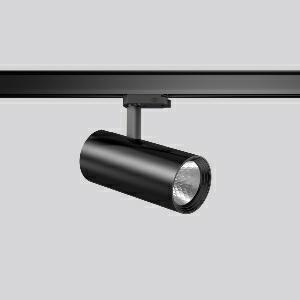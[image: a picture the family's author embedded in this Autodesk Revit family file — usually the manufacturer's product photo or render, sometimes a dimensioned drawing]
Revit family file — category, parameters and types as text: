
# Revit family: deecos_s_mini_742197_003_3_7693
name_source: partatom
category: Lighting Fixtures
units: mm (PartAtom-declared; Revit-internal decimal feet)

## family parameters
Cut with Voids When Loaded = No
Host = Face
Light Source = No
Part Type = Normal
Room Calculation Point = No
Round Connector Dimension = Use Diameter
Shared = No

## types (1)
- DEECOS S mini (1 x LED Modul 935, 2650 lm, 3500)
    Apparent Load = 20 VA
    Approval mark = CE
    CIE Flux Codes = 95 99 100 100 100
    Color Rendering = 92
    Color Temperature = 3500
    Default Elevation = 1800 mm
    Description = Series: DEECOS S mini
LED surface-mounted projector in modern design with no visible cooling ribs. Housing: die-cast aluminium, powder-coated. Rotation range: 356°. Swivel range: 90°. Black plastic ring and recessed LED to prevent glare from the side. Optical assembly with reflector made of MIRO-Silver with 98% total light reflection for outstanding efficiency - can be changed without tools. Best colour rendering index Ra>90. With multi adaptor for 3-circuit tracks 230 V. Suitable for Track on ceiling, Wall track. High quality converter without flickering and stroboscopic effect. The following accessories can be mounted without use of tools: interchangeable lenses, decorative glasses, honeycomb louvre, clear and frosted diffusers, white interchangeable plastic ring. 
Colour: deep black, matt (RAL 9005)
Diameter: 87 mm
Height: 214 mm
Lamp: LED
Socket: without socket
Colour temperature: 3500K
Colour rendering index (CRI): 92
System power: 20 W
Rated luminous flux: 2650 lm
Luminous efficiency: 133 lm/W
Control gear: Regulated power supply
Protection class: I
Type of protection: IP 20
    Height = 214 mm
    Lamp = 1 x LED Modul 935
    Lamp Light Flux = 2650 lm
    Lamp count = 1
    Length = 87 mm
    Lifetime = 50000 h
    Luminous efficacy = 133 lm/W
    Manufacturer = RZB
    ModVariant = No
    Model = 742197.003.3
    Mounting Place = Ceiling
    Mounting Type = Rail mounted
    Number of Poles = 1
    OnlyDefault = Yes
    Power Factor = 1
    Product Name = DEECOS S mini
    Product group = Track mounted projectors
    ProductGroupID = 301
    Protection Class = Protection class I
    Protection Degree = IP 20
    RLX_Detail_Level = 1
    RLX_Emergency_Light_Flux = 0 lm
    RLX_Emergency_Type = 0
    RLX_Emergency_Type_DB = No
    RlxData = <blob elided: 38909 chars, md5=da69d309>
    Socket = socket
    Standby Power = 0 W
    System Light Flux = 2650 lm
    System Power = 20 W
    Type Comments = Product without accessories
    Type Image = 741926.003.jpg
    URL = http://relux.com
    VarID = ---
    Voltage = 230 V
    Voltage Range = 220-240 V
    Weight = 0.00 kg
    Width = 0 mm  [stored 0 ft]

note: [stored X ft] marks values corroborated as IEEE doubles in the binary element streams (Revit-internal decimal feet)

## geometry (parser evidence)
native form markers: Blend x4, Sweep x10
no freeform markers — native parametric forms only
